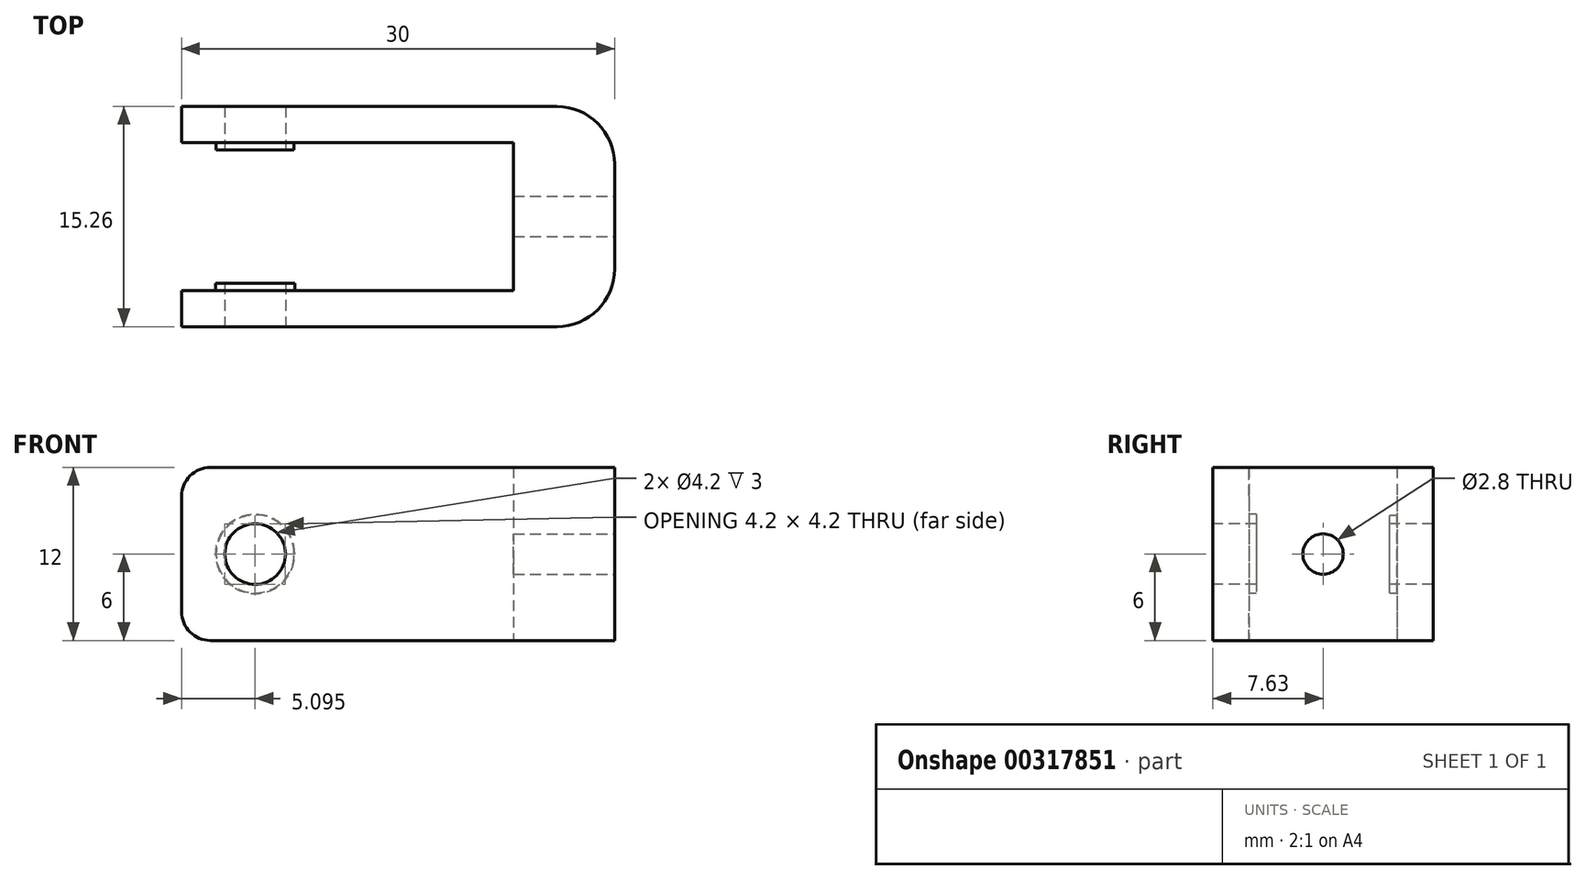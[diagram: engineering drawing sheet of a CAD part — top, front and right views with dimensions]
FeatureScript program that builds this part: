
annotation { "Feature Type Name" : "Feature", "Feature Type Description" : "" }
export const myFeature = defineFeature(function(context is Context, id is Id, definition is map)
    precondition{}
    {
        {
            var Q0;
            Q0=qCreatedBy(makeId("Top.planeOp"),FACE);
            var sketch = newSketch(context, id + "F0", { "sketchPlane" : qUnion([Q0])});
            skLineSegment(sketch, "E0", {"start": v(-23, 5.12) * mm, "end": v(-23, 7.62) * mm});
            skLineSegment(sketch, "E1", {"start": v(-23, 7.62) * mm, "end": v(7, 7.62) * mm});
            skLineSegment(sketch, "E2", {"start": v(7, 7.62) * mm, "end": v(7, -7.62) * mm});
            skLineSegment(sketch, "E3", {"start": v(7, -7.62) * mm, "end": v(-23, -7.63) * mm});
            skLineSegment(sketch, "E4", {"start": v(-23, -7.63) * mm, "end": v(-23, -5.13) * mm});
            skLineSegment(sketch, "E5", {"start": v(-23, -5.13) * mm, "end": v(0, -5.13) * mm});
            skLineSegment(sketch, "E6", {"start": v(0, -5.13) * mm, "end": v(0, 5.12) * mm});
            skLineSegment(sketch, "E7", {"start": v(0, 5.12) * mm, "end": v(-23, 5.12) * mm});
            skPoint(sketch, "E8.middle", {"position": v(0, 0) * mm});
            skSolve(sketch);
        }
        {
            var Q0;
            Q0 = qSketchRegion(id + "F0", true);
            extrude(context, id + "F1", {"entities" : qUnion([Q0]), "endBound" : BoundingType.SYMMETRIC, "depth" : 12 * mm});
        }
        {
            var Q0;
            Q0=makeQuery(id+"F1.opExtrude","SWEPT_FACE",FACE,{"disambiguationData":[OSD([sQuery(id+"F0.wireOp",EDGE,"E2")])]});
            var sketch = newSketch(context, id + "F2", { "sketchPlane" : qUnion([Q0])});
            skPoint(sketch, "E9", {"position": v(0, 0) * mm});
            skPoint(sketch, "E10", {"position": v(-9.28, 8.92) * mm});
            skSolve(sketch);
        }
        {
            var Q0;
            Q0=sQuery(id+"F2.wireOp",VERTEX,"E9");
            var Q1;
            Q1=makeQuery(id+"F1.opExtrude","SWEPT_BODY",BODY,{"disambiguationData":[OSD([sQuery(id+"F0.wireOp",EDGE,"E0"),sQuery(id+"F0.wireOp",EDGE,"E1"),sQuery(id+"F0.wireOp",EDGE,"E2"),sQuery(id+"F0.wireOp",EDGE,"E3"),sQuery(id+"F0.wireOp",EDGE,"E4"),sQuery(id+"F0.wireOp",EDGE,"E5"),sQuery(id+"F0.wireOp",EDGE,"E6"),sQuery(id+"F0.wireOp",EDGE,"E7")])]});
            hole(context, id + "F3", {"style" : HoleStyle.SIMPLE, "endStyle" : HoleEndStyle.THROUGH, "holeDiameter" : 2.8 * mm, "tappedDepth" : 12 * mm, "tapClearance" : 3, "locations" : qUnion([Q0]), "scope" : qUnion([Q1])});
        }
        {
            var Q0;
            Q0=makeQuery(id+"F1.opExtrude","SWEPT_FACE",FACE,{"disambiguationData":[OSD([sQuery(id+"F0.wireOp",EDGE,"E3")])]});
            var sketch = newSketch(context, id + "F4", { "sketchPlane" : qUnion([Q0])});
            skPoint(sketch, "E11", {"position": v(-17.9, 0) * mm});
            skLineSegment(sketch, "E12", {"start": v(-23, 0.93) * mm, "end": v(-18, 0.93) * mm, "construction": true});
            skSolve(sketch);
        }
        {
            var Q0;
            Q0=sQuery(id+"F4.wireOp",VERTEX,"E11");
            var Q1;
            Q1=makeQuery(id+"F1.opExtrude","SWEPT_BODY",BODY,{"disambiguationData":[OSD([sQuery(id+"F0.wireOp",EDGE,"E0"),sQuery(id+"F0.wireOp",EDGE,"E1"),sQuery(id+"F0.wireOp",EDGE,"E2"),sQuery(id+"F0.wireOp",EDGE,"E3"),sQuery(id+"F0.wireOp",EDGE,"E4"),sQuery(id+"F0.wireOp",EDGE,"E5"),sQuery(id+"F0.wireOp",EDGE,"E6"),sQuery(id+"F0.wireOp",EDGE,"E7")])]});
            hole(context, id + "F5", {"style" : HoleStyle.SIMPLE, "endStyle" : HoleEndStyle.BLIND, "holeDiameter" : 4.2 * mm, "holeDepth" : 20 * mm, "tappedDepth" : 12 * mm, "tapClearance" : 3, "locations" : qUnion([Q0]), "scope" : qUnion([Q1])});
        }
        {
            var Q0;
            Q0=makeQuery(id+"F1.opExtrude","SWEPT_FACE",FACE,{"disambiguationData":[OSD([sQuery(id+"F0.wireOp",EDGE,"E5")])]});
            var sketch = newSketch(context, id + "F6", { "sketchPlane" : qUnion([Q0])});
            skCircle(sketch, "E13.0", {"center": v(17.9, 0) * mm, "radius": 2.1 * mm});
            skCircle(sketch, "E14", {"center": v(17.9, 0) * mm, "radius": 2.75 * mm});
            skSolve(sketch);
        }
        {
            var Q0;
            Q0 = qSketchRegion(id + "F6", true);
            extrude(context, id + "F7", {"entities" : qUnion([Q0]), "operationType" : NewBodyOperationType.ADD, "depth" : .5 * mm});
        }
        {
            var Q0;
            Q0=makeQuery(id+"F1.opExtrude","SWEPT_FACE",FACE,{"disambiguationData":[OSD([sQuery(id+"F0.wireOp",EDGE,"E7")])]});
            var sketch = newSketch(context, id + "F8", { "sketchPlane" : qUnion([Q0])});
            skCircle(sketch, "E15.0", {"center": v(-17.9, 0) * mm, "radius": 2.1 * mm});
            skCircle(sketch, "E16", {"center": v(-17.9, 0) * mm, "radius": 2.7 * mm});
            skSolve(sketch);
        }
        {
            var Q0;
            Q0 = qSketchRegion(id + "F8", true);
            extrude(context, id + "F9", {"entities" : qUnion([Q0]), "operationType" : NewBodyOperationType.ADD, "depth" : .5 * mm});
        }
        {
            var Q0;
            Q0=makeQuery(id+"F1.opExtrude","SWEPT_EDGE",EDGE,{"disambiguationData":[OSD([sQuery(id+"F0.wireOp",EDGE,"E2"),sQuery(id+"F0.wireOp",EDGE,"E3")])]});
            var Q1;
            Q1=makeQuery(id+"F1.opExtrude","SWEPT_EDGE",EDGE,{"disambiguationData":[OSD([sQuery(id+"F0.wireOp",EDGE,"E1"),sQuery(id+"F0.wireOp",EDGE,"E2")])]});
            fillet(context, id + "F10", {"entities" : qUnion([Q0, Q1]), "radius" : 4 * mm, "tangentPropagation" : true, "allowEdgeOverflow" : false});
        }
        {
            var Q0;
            Q0=makeQuery(id+"F1.opExtrude","CAP_EDGE",EDGE,{"disambiguationData":[OSD([sQuery(id+"F0.wireOp",EDGE,"E4")])],"isStart":false});
            var Q1;
            Q1=makeQuery(id+"F1.opExtrude","CAP_EDGE",EDGE,{"disambiguationData":[OSD([sQuery(id+"F0.wireOp",EDGE,"E0")])],"isStart":false});
            var Q2;
            Q2=makeQuery(id+"F1.opExtrude","CAP_EDGE",EDGE,{"disambiguationData":[OSD([sQuery(id+"F0.wireOp",EDGE,"E0")])],"isStart":true});
            var Q3;
            Q3=makeQuery(id+"F1.opExtrude","CAP_EDGE",EDGE,{"disambiguationData":[OSD([sQuery(id+"F0.wireOp",EDGE,"E4")])],"isStart":true});
            fillet(context, id + "F11", {"entities" : qUnion([Q0, Q1, Q2, Q3]), "radius" : 2 * mm, "tangentPropagation" : true, "allowEdgeOverflow" : false});
        }
    });
